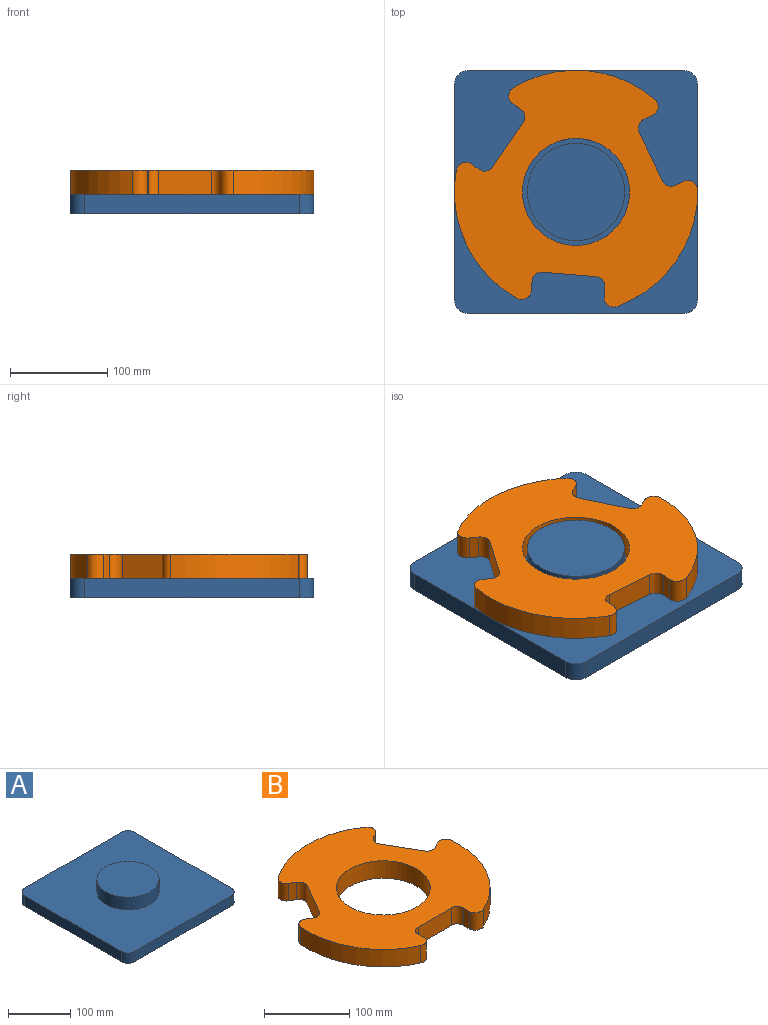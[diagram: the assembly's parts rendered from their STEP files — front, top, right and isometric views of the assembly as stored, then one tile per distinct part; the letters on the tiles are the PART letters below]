
ASSEMBLY  parts=2 mates=1
PART A: 12 faces, bbox 250x250x45 mm
  f0: plane 220x20mm, normal (1,0,0), area 4400mm2, adj f4,f5,f8,f11
  f1: plane 220x20mm, normal (0,1,0), area 4400mm2, adj f4,f5,f8,f9
  f2: plane 220x20mm, normal (-1,0,0), area 4400mm2, adj f4,f5,f9,f10
  f3: plane 220x20mm, normal (0,-1,0), area 4400mm2, adj f4,f5,f10,f11
  f4: plane 250x250mm, normal (0,0,1), area 54452.9mm2, adj f0,f1,f2,f3,f6,f8,f9,f10
  f5: plane 250x250mm, normal (0,0,-1), area 62306.9mm2, adj f0,f1,f2,f3,f8,f9,f10,f11
  f6: cylinder r=50mm len=100mm, axis (0,0,-1), area 7854mm2, adj f4,f7
  f7: plane 100x100mm, normal (0,0,1), area 7854mm2, adj f6
  f8: cylinder r=15mm len=20mm, axis (0,0,-1), area 471.2mm2, adj f0,f1,f4,f5
  f9: cylinder r=15mm len=20mm, axis (0,0,1), area 471.2mm2, adj f1,f2,f4,f5
  f10: cylinder r=15mm len=20mm, axis (0,0,-1), area 471.2mm2, adj f2,f3,f4,f5
  f11: cylinder r=15mm len=20mm, axis (0,0,1), area 471.2mm2, adj f0,f3,f4,f5
PART B: 27 faces, bbox 250x239.7x25 mm
  f0: plane 250x239.73mm, normal (0,0,1), area 30837.4mm2, adj f2,f3,f4,f5,f6,f7,f8,f9
  f1: plane 250x239.73mm, normal (0,0,-1), area 30837.4mm2, adj f2,f3,f4,f5,f6,f7,f8,f9
  f2: cylinder r=125mm len=145.54mm, axis (0,0,-1), area 3883.8mm2, adj f0,f1,f18,f26
  f3: cylinder r=125mm len=126.05mm, axis (0,0,-1), area 3883.8mm2, adj f0,f1,f11,f19
  f4: cylinder r=55mm len=110mm, axis (0,0,-1), area 8639.4mm2, adj f0,f1
  f5: cylinder r=125mm len=126.05mm, axis (0,0,-1), area 3883.8mm2, adj f0,f1,f12,f25
  f6: plane 25x9.73mm, normal (-1,0,0), area 243.3mm2, adj f0,f1,f9,f12
  f7: plane 55x25mm, normal (0,-1,0), area 1375mm2, adj f0,f1,f9,f10
  f8: plane 25x9.73mm, normal (1,0,0), area 243.3mm2, adj f0,f1,f10,f11
  f9: cylinder r=10mm len=25mm, axis (0,0,-1), area 392.7mm2, adj f0,f1,f6,f7
  f10: cylinder r=10mm len=25mm, axis (0,0,-1), area 392.7mm2, adj f0,f1,f7,f8
  f11: cylinder r=10mm len=25mm, axis (0,0,-1), area 499.1mm2, adj f0,f1,f3,f8
  f12: cylinder r=10mm len=25mm, axis (0,0,-1), area 499.1mm2, adj f0,f1,f5,f6
  f13: plane 25x8.43mm, normal (0.5,0.87,0), area 243.3mm2, adj f0,f1,f16,f19
  f14: plane 47.63x27.5mm, normal (-0.87,0.5,0), area 1375mm2, adj f0,f1,f16,f17
  f15: plane 25x8.43mm, normal (-0.5,-0.87,0), area 243.3mm2, adj f0,f1,f17,f18
  f16: cylinder r=10mm len=25mm, axis (0,0,-1), area 392.7mm2, adj f0,f1,f13,f14
  f17: cylinder r=10mm len=25mm, axis (0,0,-1), area 392.7mm2, adj f0,f1,f14,f15
  f18: cylinder r=10mm len=25mm, axis (0,0,-1), area 499.1mm2, adj f0,f1,f2,f15
  f19: cylinder r=10mm len=25mm, axis (0,0,-1), area 499.1mm2, adj f0,f1,f3,f13
  f20: plane 25x8.43mm, normal (0.5,-0.87,0), area 243.3mm2, adj f0,f1,f23,f26
  f21: plane 47.63x27.5mm, normal (0.87,0.5,0), area 1375mm2, adj f0,f1,f23,f24
  f22: plane 25x8.43mm, normal (-0.5,0.87,0), area 243.3mm2, adj f0,f1,f24,f25
  f23: cylinder r=10mm len=25mm, axis (0,0,-1), area 392.7mm2, adj f0,f1,f20,f21
  f24: cylinder r=10mm len=25mm, axis (0,0,-1), area 392.7mm2, adj f0,f1,f21,f22
  f25: cylinder r=10mm len=25mm, axis (0,0,-1), area 499.1mm2, adj f0,f1,f5,f22
  f26: cylinder r=10mm len=25mm, axis (0,0,-1), area 499.1mm2, adj f0,f1,f2,f20
PLACE A at identity fixed
PLACE B rot(axis=(0,0,1),115.3deg) t=(0,0,0)mm
MATE revolute A.f6 <-> B.f2  axis (0,0,1) through (0,0,45)mm
